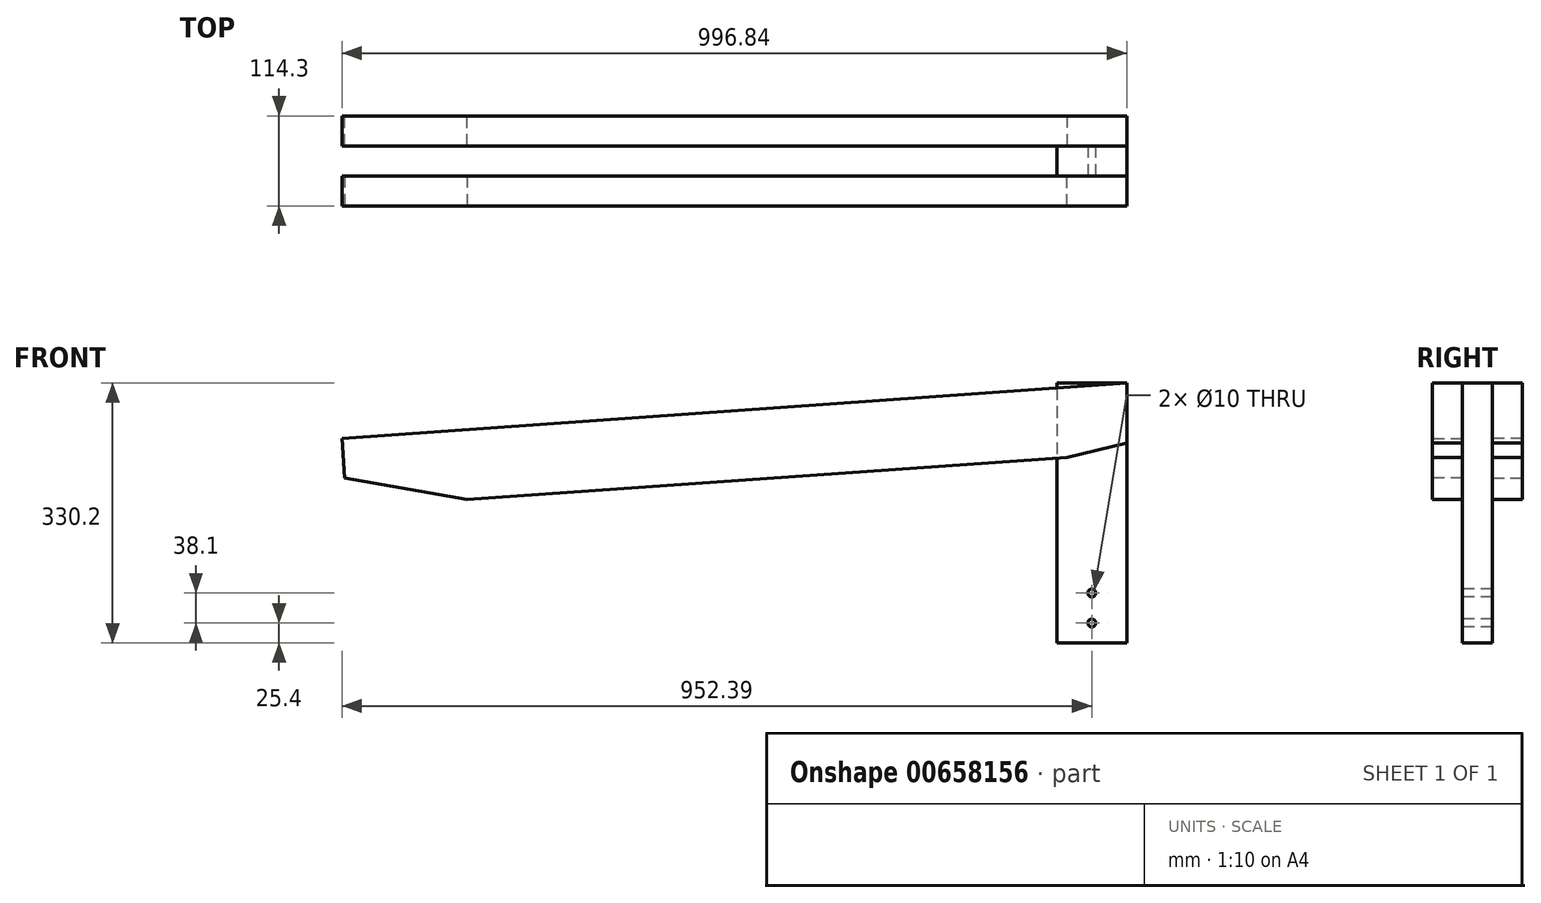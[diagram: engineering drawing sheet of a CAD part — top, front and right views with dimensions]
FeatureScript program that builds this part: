
annotation { "Feature Type Name" : "Feature", "Feature Type Description" : "" }
export const myFeature = defineFeature(function(context is Context, id is Id, definition is map)
    precondition{}
    {
        {
            var Q0;
            Q0=qCreatedBy(makeId("Top.planeOp"),FACE);
            var sketch = newSketch(context, id + "F0", { "sketchPlane" : qUnion([Q0])});
            skLineSegment(sketch, "E0.bottom", {"start": v(0, 0) * mm, "end": v(88.9, 0) * mm});
            skLineSegment(sketch, "E0.top", {"start": v(0, 38.1) * mm, "end": v(88.9, 38.1) * mm});
            skLineSegment(sketch, "E0.left", {"start": v(0, 0) * mm, "end": v(0, 38.1) * mm});
            skLineSegment(sketch, "E0.right", {"start": v(88.9, 0) * mm, "end": v(88.9, 38.1) * mm});
            skSolve(sketch);
        }
        {
            var Q0;
            Q0=makeQuery(id+"F0.imprint","IMPRINT",FACE,{"disambiguationData":[TD([[makeQuery(id+"F0.imprint","IMPRINT",EDGE,{"derivedFrom":sQuery(id+"F0.wireOp",EDGE,"E0.bottom")}),1.0]])]});
            extrude(context, id + "F1", {"entities" : qUnion([Q0]), "depth" : 330.2 * mm, "offsetDistance" : 25.4 * mm});
        }
        {
            var Q0;
            Q0=makeQuery(id+"F1.opExtrude","SWEPT_FACE",FACE,{"disambiguationData":[OSD([sQuery(id+"F0.wireOp",EDGE,"E0.bottom")])]});
            var sketch = newSketch(context, id + "F2", { "sketchPlane" : qUnion([Q0])});
            skPoint(sketch, "E1", {"position": v(44.45, 25.4) * mm});
            skPoint(sketch, "E1.positionSnap0", {"position": v(44.45, 0) * mm});
            skPoint(sketch, "E2", {"position": v(44.45, 63.5) * mm});
            skSolve(sketch);
        }
        {
            var Q0;
            Q0=sQuery(id+"F2.wireOp",VERTEX,"E2");
            var Q1;
            Q1=sQuery(id+"F2.wireOp",VERTEX,"E1");
            var Q2;
            Q2=makeQuery(id+"F1.opExtrude","SWEPT_BODY",BODY,{"disambiguationData":[OSD([sQuery(id+"F0.wireOp",EDGE,"E0.bottom"),sQuery(id+"F0.wireOp",EDGE,"E0.top"),sQuery(id+"F0.wireOp",EDGE,"E0.left"),sQuery(id+"F0.wireOp",EDGE,"E0.right")])]});
            hole(context, id + "F3", {"style" : HoleStyle.SIMPLE, "endStyle" : HoleEndStyle.THROUGH, "holeDiameter" : 10 * mm, "majorDiameter" : 6.35 * mm, "isTappedThrough" : true, "tappedDepth" : 12.7 * mm, "tapClearance" : 3, "locations" : qUnion([Q0, Q1]), "scope" : qUnion([Q2])});
        }
        {
            var Q0;
            Q0=makeQuery(id+"F1.opExtrude","SWEPT_FACE",FACE,{"disambiguationData":[OSD([sQuery(id+"F0.wireOp",EDGE,"E0.bottom")])]});
            var sketch = newSketch(context, id + "F4", { "sketchPlane" : qUnion([Q0])});
            skLineSegment(sketch, "E3", {"start": v(88.9, 330.2) * mm, "end": v(-907.94, 260) * mm});
            skLineSegment(sketch, "E4", {"start": v(-907.94, 260) * mm, "end": v(-901.7, 171.33) * mm});
            skLineSegment(sketch, "E5", {"start": v(-901.7, 171.33) * mm, "end": v(12.7, 235.71) * mm});
            skLineSegment(sketch, "E6", {"start": v(12.7, 235.71) * mm, "end": v(88.9, 254) * mm});
            skLineSegment(sketch, "E7", {"start": v(88.9, 254) * mm, "end": v(88.9, 330.2) * mm});
            skSolve(sketch);
        }
        {
            var Q0;
            {var subQ1=sQuery(id+"F4.wireOp",EDGE,"E6");Q0=makeQuery(id+"F4.imprint","IMPRINT",FACE,{"disambiguationData":[TD([[makeQuery(id+"F4.imprint","IMPRINT",EDGE,{"derivedFrom":subQ1}),1.0]])]});}
            var Q1;
            {var subQ0=sQuery(id+"F4.wireOp",EDGE,"E4");Q1=makeQuery(id+"F4.imprint","IMPRINT",FACE,{"disambiguationData":[TD([[makeQuery(id+"F4.imprint","IMPRINT",EDGE,{"derivedFrom":subQ0}),1.0]])]});}
            extrude(context, id + "F5", {"entities" : qUnion([Q0, Q1]), "depth" : 38.1 * mm, "offsetDistance" : 25.4 * mm});
        }
        {
            var Q0;
            Q0=makeQuery(id+"F1.opExtrude","SWEPT_FACE",FACE,{"disambiguationData":[OSD([sQuery(id+"F0.wireOp",EDGE,"E0.bottom")])]});
            cPlane(context, id + "F6", {"entities" : qUnion([Q0]), "cplaneType" : CPlaneType.OFFSET, "offset" : 19.05 * mm, "oppositeDirection" : true, "width" : 152.4 * mm, "height" : 152.4 * mm});
        }
        {
            var Q0;
            Q0=makeQuery(id+"F5.opExtrude","CAP_FACE",FACE,{"disambiguationData":[OSD([sQuery(id+"F4.wireOp",EDGE,"E3"),sQuery(id+"F4.wireOp",EDGE,"E4"),sQuery(id+"F4.wireOp",EDGE,"E5"),sQuery(id+"F4.wireOp",EDGE,"E6"),sQuery(id+"F4.wireOp",EDGE,"E7")])],"isStart":false});
            var sketch = newSketch(context, id + "F7", { "sketchPlane" : qUnion([Q0])});
            skLineSegment(sketch, "E8", {"start": v(-901.7, 171.33) * mm, "end": v(-749.3, 182.06) * mm});
            skLineSegment(sketch, "E9", {"start": v(-749.3, 182.06) * mm, "end": v(-904.38, 209.43) * mm});
            skLineSegment(sketch, "E10", {"start": v(-904.38, 209.43) * mm, "end": v(-901.7, 171.33) * mm});
            skSolve(sketch);
        }
        {
            var Q0;
            Q0=makeQuery(id+"F7.imprint","IMPRINT",FACE,{"disambiguationData":[TD([[makeQuery(id+"F7.imprint","IMPRINT",EDGE,{"derivedFrom":sQuery(id+"F7.wireOp",EDGE,"E8")}),1.0]])]});
            extrude(context, id + "F8", {"entities" : qUnion([Q0]), "operationType" : NewBodyOperationType.REMOVE, "endBound" : BoundingType.THROUGH_ALL, "oppositeDirection" : true, "depth" : 228.6 * mm, "offsetDistance" : 25.4 * mm});
        }
        {
            var Q0;
            Q0=makeQuery(id+"F5.opExtrude","SWEPT_BODY",BODY,{"disambiguationData":[OSD([sQuery(id+"F4.wireOp",EDGE,"E3"),sQuery(id+"F4.wireOp",EDGE,"E4"),sQuery(id+"F4.wireOp",EDGE,"E5"),sQuery(id+"F4.wireOp",EDGE,"E6"),sQuery(id+"F4.wireOp",EDGE,"E7")])]});
            var Q1;
            Q1=qCreatedBy(id+"F6.planeOp",FACE);
            mirror(context, id + "F9", {"entities" : qUnion([Q0]), "mirrorPlane" : qUnion([Q1])});
        }
    });
